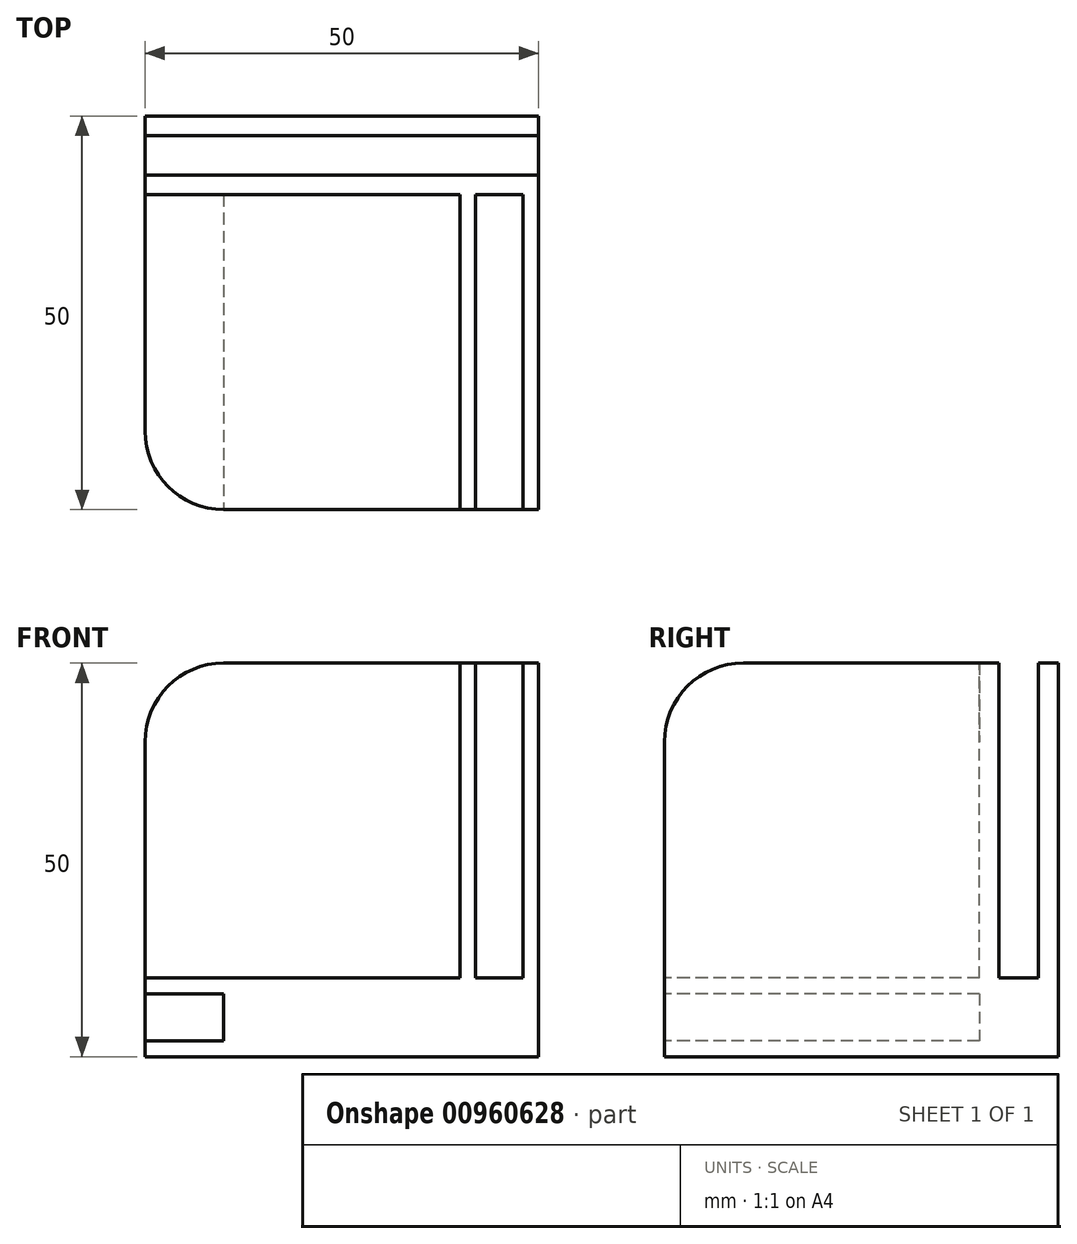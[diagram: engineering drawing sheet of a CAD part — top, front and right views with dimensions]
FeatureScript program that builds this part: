
annotation { "Feature Type Name" : "Feature", "Feature Type Description" : "" }
export const myFeature = defineFeature(function(context is Context, id is Id, definition is map)
    precondition{}
    {
        {
            var Q0;
            Q0=qCreatedBy(makeId("Top.planeOp"),FACE);
            var sketch = newSketch(context, id + "F0", { "sketchPlane" : qUnion([Q0])});
            skLineSegment(sketch, "E0.bottom", {"start": v(0, 0) * mm, "end": v(-50, 0) * mm});
            skLineSegment(sketch, "E0.top", {"start": v(0, -50) * mm, "end": v(-40, -50) * mm});
            skLineSegment(sketch, "E0.left", {"start": v(0, 0) * mm, "end": v(0, -50) * mm});
            skLineSegment(sketch, "E0.right", {"start": v(-50, 0) * mm, "end": v(-50, -40) * mm});
            skPoint(sketch, "E1.visualSharp", {"position": v(-50, -50) * mm});
            skArc(sketch, "E1.filletArc", {"start": v(-50, -40) * mm, "mid": v(-47.07, -47.07) * mm, "end": v(-40, -50) * mm});
            skSolve(sketch);
        }
        {
            var Q0;
            Q0=makeQuery(id+"F0.imprint","IMPRINT",FACE,{"disambiguationData":[TD([[makeQuery(id+"F0.imprint","IMPRINT",EDGE,{"derivedFrom":sQuery(id+"F0.wireOp",EDGE,"tNkWgY0K-5FoM-fzsk-HCrw-KOSka2LcS9h1.bottom")}),-1.0]])]});
            var Q1;
            Q1=makeQuery(id+"F0.imprint","IMPRINT",FACE,{"disambiguationData":[TD([[makeQuery(id+"F0.imprint","IMPRINT",EDGE,{"derivedFrom":sQuery(id+"F0.wireOp",EDGE,"E0.bottom")}),1.0]])]});
            var Q2;
            Q2=makeQuery(id+"F0.imprint","IMPRINT",FACE,{"disambiguationData":[TD([[makeQuery(id+"F0.imprint","IMPRINT",EDGE,{"derivedFrom":sQuery(id+"F0.wireOp",EDGE,"E0.top")}),-1.0]])]});
            var Q3;
            Q3=makeQuery(id+"F0.imprint","IMPRINT",FACE,{"disambiguationData":[TD([[makeQuery(id+"F0.imprint","IMPRINT",EDGE,{"derivedFrom":sQuery(id+"F0.wireOp",EDGE,"fvIwUqZD-S5C8-yHxi-N0ak-uGxWySerV2bo.bottom")}),1.0]])]});
            var Q4;
            Q4=makeQuery(id+"F0.imprint","IMPRINT",FACE,{"disambiguationData":[TD([[makeQuery(id+"F0.imprint","IMPRINT",EDGE,{"derivedFrom":sQuery(id+"F0.wireOp",EDGE,"JSCxDXyh-nDxv-V0qH-dKlW-7TGNpykFalIj.bottom")}),1.0]])]});
            extrude(context, id + "F1", {"entities" : qUnion([Q0, Q1, Q2, Q3, Q4]), "depth" : 10 * mm, "offsetDistance" : 25 * mm});
        }
        {
            var Q0;
            Q0=qCreatedBy(makeId("Right.planeOp"),FACE);
            var sketch = newSketch(context, id + "F2", { "sketchPlane" : qUnion([Q0])});
            skLineSegment(sketch, "E2.bottom", {"start": v(0, 10) * mm, "end": v(-50, 10) * mm});
            skLineSegment(sketch, "E2.top", {"start": v(0, 50) * mm, "end": v(-40, 50) * mm});
            skLineSegment(sketch, "E2.left", {"start": v(0, 10) * mm, "end": v(0, 50) * mm});
            skLineSegment(sketch, "E2.right", {"start": v(-50, 10) * mm, "end": v(-50, 40) * mm});
            skPoint(sketch, "E3.visualSharp", {"position": v(-50, 50) * mm});
            skArc(sketch, "E3.filletArc", {"start": v(-40, 50) * mm, "mid": v(-47.07, 47.07) * mm, "end": v(-50, 40) * mm});
            skSolve(sketch);
        }
        {
            var Q0;
            Q0=makeQuery(id+"F2.imprint","IMPRINT",FACE,{"disambiguationData":[TD([[makeQuery(id+"F2.imprint","IMPRINT",EDGE,{"derivedFrom":sQuery(id+"F2.wireOp",EDGE,"E2.bottom")}),-1.0]])]});
            extrude(context, id + "F3", {"entities" : qUnion([Q0]), "operationType" : NewBodyOperationType.ADD, "oppositeDirection" : true, "depth" : 10 * mm, "offsetDistance" : 25 * mm});
        }
        {
            var Q0;
            Q0=qCreatedBy(makeId("Front.planeOp"),FACE);
            var sketch = newSketch(context, id + "F4", { "sketchPlane" : qUnion([Q0])});
            skLineSegment(sketch, "E4.bottom", {"start": v(-10, 10) * mm, "end": v(-50, 10) * mm});
            skLineSegment(sketch, "E4.top", {"start": v(-10, 50) * mm, "end": v(-40, 50) * mm});
            skLineSegment(sketch, "E4.left", {"start": v(-10, 10) * mm, "end": v(-10, 50) * mm});
            skLineSegment(sketch, "E4.right", {"start": v(-50, 10) * mm, "end": v(-50, 40) * mm});
            skPoint(sketch, "E5.visualSharp", {"position": v(-50, 50) * mm});
            skArc(sketch, "E5.filletArc", {"start": v(-40, 50) * mm, "mid": v(-47.07, 47.07) * mm, "end": v(-50, 40) * mm});
            skSolve(sketch);
        }
        {
            var Q0;
            Q0=makeQuery(id+"F4.imprint","IMPRINT",FACE,{"disambiguationData":[TD([[makeQuery(id+"F4.imprint","IMPRINT",EDGE,{"derivedFrom":sQuery(id+"F4.wireOp",EDGE,"E4.bottom")}),-1.0]])]});
            extrude(context, id + "F5", {"entities" : qUnion([Q0]), "operationType" : NewBodyOperationType.ADD, "depth" : 10 * mm, "offsetDistance" : 25 * mm});
        }
        {
            var Q0;
            Q0=makeQuery(id+"F3.boolean.opBoolean","MERGE",FACE,{"derivedFrom":[makeQuery(id+"F1.opExtrude","SWEPT_FACE",FACE,{"disambiguationData":[OSD([sQuery(id+"F0.wireOp",EDGE,"E0.top")])]}),makeQuery(id+"F3.opExtrude","SWEPT_FACE",FACE,{"disambiguationData":[OSD([sQuery(id+"F2.wireOp",EDGE,"E2.right")])]})]});
            var sketch = newSketch(context, id + "F6", { "sketchPlane" : qUnion([Q0])});
            skLineSegment(sketch, "E6.bottom", {"start": v(-10, 2) * mm, "end": v(-60, 2) * mm});
            skLineSegment(sketch, "E6.top", {"start": v(-10, 8) * mm, "end": v(-60, 8) * mm});
            skLineSegment(sketch, "E6.left", {"start": v(-10, 2) * mm, "end": v(-10, 8) * mm});
            skLineSegment(sketch, "E6.right", {"start": v(-60, 2) * mm, "end": v(-60, 8) * mm});
            skLineSegment(sketch, "E7.bottom", {"start": v(-10, 2) * mm, "end": v(-15, 2) * mm});
            skLineSegment(sketch, "E7.top", {"start": v(-10, 52) * mm, "end": v(-15, 52) * mm});
            skLineSegment(sketch, "E8.bottom", {"start": v(-2, 10) * mm, "end": v(-8, 10) * mm});
            skLineSegment(sketch, "E8.top", {"start": v(-2, 60) * mm, "end": v(-8, 60) * mm});
            skLineSegment(sketch, "E8.left", {"start": v(-2, 10) * mm, "end": v(-2, 60) * mm});
            skLineSegment(sketch, "E8.right", {"start": v(-8, 10) * mm, "end": v(-8, 60) * mm});
            skSolve(sketch);
        }
        {
            var Q0;
            {var subQ5=sQuery(id+"F6.wireOp",EDGE,"E7.bottom");Q0=makeQuery(id+"F6.imprint","IMPRINT",FACE,{"disambiguationData":[TD([[makeQuery(id+"F6.imprint","IMPRINT",EDGE,{"derivedFrom":subQ5}),-1.0]])]});}
            var Q1;
            {var subQ0=sQuery(id+"F6.wireOp",EDGE,"E7.right");var subQ5=sQuery(id+"F6.wireOp",EDGE,"E6.top");var subQ7=makeQuery(id+"F6.imprint","INTERSECT",VERTEX,{"derivedFrom":[subQ5,subQ0]});Q1=makeQuery(id+"F6.imprint","IMPRINT",FACE,{"disambiguationData":[TD([[makeQuery(id+"F6.imprint","IMPRINT",EDGE,{"disambiguationData":[TD([[subQ7,-1.0]])],"derivedFrom":subQ5}),1.0]])]});}
            var Q2;
            {var subQ0=sQuery(id+"F6.wireOp",EDGE,"E6.right");Q2=makeQuery(id+"F6.imprint","IMPRINT",FACE,{"disambiguationData":[TD([[makeQuery(id+"F6.imprint","IMPRINT",EDGE,{"derivedFrom":subQ0}),-1.0]])]});}
            var Q3;
            {var subQ0=sQuery(id+"F6.wireOp",EDGE,"E8.bottom");Q3=makeQuery(id+"F6.imprint","IMPRINT",FACE,{"disambiguationData":[TD([[makeQuery(id+"F6.imprint","IMPRINT",EDGE,{"derivedFrom":subQ0}),-1.0]])]});}
            var Q4;
            {var subQ0=sQuery(id+"F6.wireOp",EDGE,"E8.top");Q4=makeQuery(id+"F6.imprint","IMPRINT",FACE,{"disambiguationData":[TD([[makeQuery(id+"F6.imprint","IMPRINT",EDGE,{"derivedFrom":subQ0}),1.0]])]});}
            extrude(context, id + "F7", {"entities" : qUnion([Q0, Q1, Q2, Q3, Q4]), "operationType" : NewBodyOperationType.REMOVE, "oppositeDirection" : true, "depth" : 40 * mm, "offsetDistance" : 25 * mm});
        }
        {
            var Q0;
            Q0=makeQuery(id+"F5.boolean.opBoolean","MERGE",FACE,{"derivedFrom":[makeQuery(id+"F3.opExtrude","SWEPT_FACE",FACE,{"disambiguationData":[OSD([sQuery(id+"F2.wireOp",EDGE,"E2.top")])]}),makeQuery(id+"F5.opExtrude","SWEPT_FACE",FACE,{"disambiguationData":[OSD([sQuery(id+"F4.wireOp",EDGE,"E4.top")])]})]});
            var sketch = newSketch(context, id + "F8", { "sketchPlane" : qUnion([Q0])});
            skLineSegment(sketch, "E9.bottom", {"start": v(5, -2.5) * mm, "end": v(-55, -2.5) * mm});
            skLineSegment(sketch, "E9.top", {"start": v(5, -7.5) * mm, "end": v(-55, -7.5) * mm});
            skLineSegment(sketch, "E9.left", {"start": v(5, -2.5) * mm, "end": v(5, -7.5) * mm});
            skLineSegment(sketch, "E9.right", {"start": v(-55, -2.5) * mm, "end": v(-55, -7.5) * mm});
            skSolve(sketch);
        }
        {
            var Q0;
            {var subQ0=sQuery(id+"F8.wireOp",EDGE,"E9.left");Q0=makeQuery(id+"F8.imprint","IMPRINT",FACE,{"disambiguationData":[TD([[makeQuery(id+"F8.imprint","IMPRINT",EDGE,{"derivedFrom":subQ0}),-1.0]])]});}
            var Q1;
            {var subQ0=sQuery(id+"F8.wireOp",EDGE,"E9.right");Q1=makeQuery(id+"F8.imprint","IMPRINT",FACE,{"disambiguationData":[TD([[makeQuery(id+"F8.imprint","IMPRINT",EDGE,{"derivedFrom":subQ0}),1.0]])]});}
            var Q2;
            {var subQ0=sQuery(id+"F8.wireOp",EDGE,"E9.bottom");var subQ1=makeQuery(id+"F3.opExtrude","CAP_EDGE",EDGE,{"disambiguationData":[OSD([sQuery(id+"F2.wireOp",EDGE,"E2.top")])],"isStart":true});var subQ2=makeQuery(id+"F8.imprint","INTERSECT",VERTEX,{"derivedFrom":[subQ1,subQ0]});Q2=makeQuery(id+"F8.imprint","IMPRINT",FACE,{"disambiguationData":[TD([[makeQuery(id+"F8.imprint","IMPRINT",EDGE,{"disambiguationData":[TD([[subQ2,-1.0]])],"derivedFrom":subQ1}),-1.0]])]});}
            extrude(context, id + "F9", {"entities" : qUnion([Q0, Q1, Q2]), "operationType" : NewBodyOperationType.REMOVE, "oppositeDirection" : true, "depth" : 40 * mm, "offsetDistance" : 25 * mm});
        }
    });
